# Revit family: Toilet_Round-Front-American_Standard-Cadet_Pro-215BB_Series
name_source: partatom
category: Plumbing Fixtures
revit_build: Autodesk Revit 2014 (Build: 20130308_1515(x64)
units: mm (PartAtom-declared; Revit-internal decimal feet)

## types (2) — shared parameters
ADA Compliant = Yes
Assembly Code = D2010110
Bowl Shape = Round Front
CW Connection = Yes
CWFU = 5
Cold Water Connection Diameter = 3/8"
Cold Water Connection Height = 10"
Cold Water Connection Radius = 3/16"
Cold Water Connection Width = 6"
Default Elevation = 0"
HW Connection = No
Height = 30 3/8"
Installation Type = Floor Mounted
Length = 26 1/4"
Manufacturer = American Standard
Material = Vitreous China-American Standard-020-White
Price = Prices may vary. Please consult Manufacturer Representative for most up-to-date price list.
Product Documentation Link = https://www.americanstandard-us.com
Product Page URL = https://www.americanstandard-us.com
URL = http://www.americanstandard-us.com
Vent Connection = No
WFU = 5
Waste Connection = Yes
Waste Connection Diameter = 2 1/8"
Waste Connection Radius = 1 1/16"
Width = 18 1/8"
zero-valued in all types: HWFU

## per-type parameters (varying)
| type | Description | Flush Rate |
| 215BB.004 | Cadet PRO Right Height Round Front Toilet 10" Rough-In 1.6gpf,Right hand trip lever - White | 1.6 gpf(6.0Lpf) |
| 215BB.104 | Cadet PRO Right Height Round Front Toilet 10" Rough-In. | 1.28 gpf(4.8Lpf) |

note: column(s) folded — value = type name in every type: Model

## geometry (parser evidence)
native form markers: Sweep x2
no freeform markers — native parametric forms only
